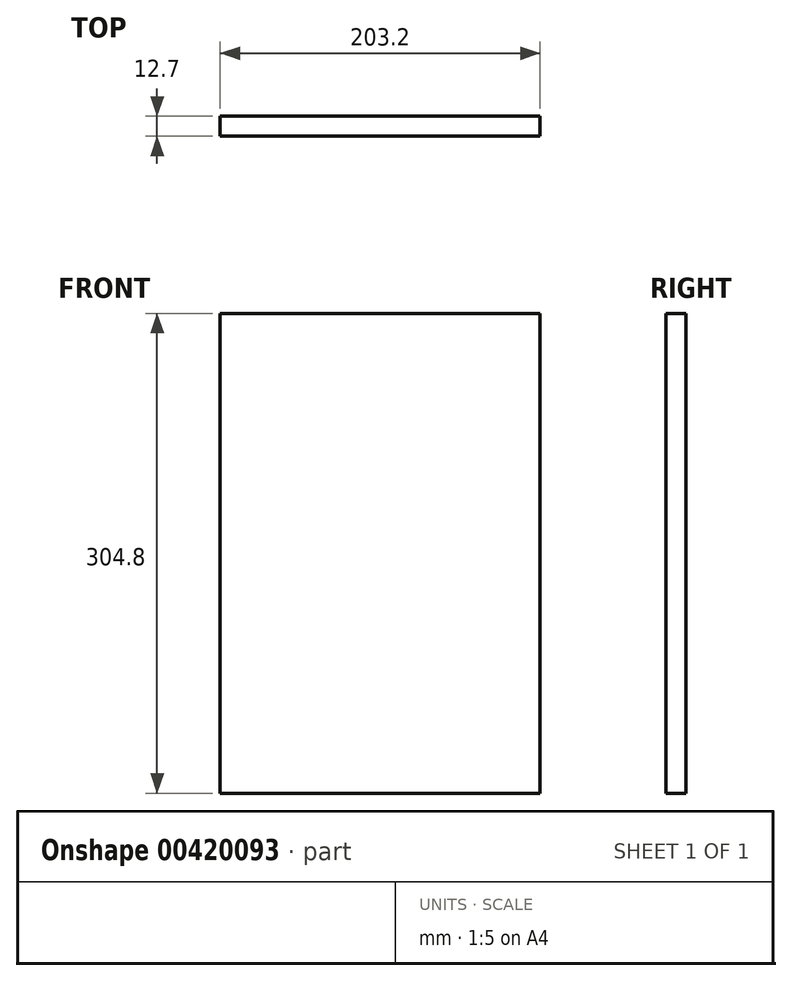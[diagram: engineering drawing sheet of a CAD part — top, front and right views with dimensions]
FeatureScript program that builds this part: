
annotation { "Feature Type Name" : "Feature", "Feature Type Description" : "" }
export const myFeature = defineFeature(function(context is Context, id is Id, definition is map)
    precondition{}
    {
        {
            var Q0;
            Q0=qCreatedBy(makeId("Front.planeOp"),FACE);
            var sketch = newSketch(context, id + "F0", { "sketchPlane" : qUnion([Q0])});
            skLineSegment(sketch, "E0.bottom", {"start": v(-107.05, 246.5) * mm, "end": v(96.15, 246.5) * mm});
            skLineSegment(sketch, "E0.top", {"start": v(-107.05, -58.3) * mm, "end": v(96.15, -58.3) * mm});
            skLineSegment(sketch, "E0.left", {"start": v(-107.05, 246.5) * mm, "end": v(-107.05, -58.3) * mm});
            skLineSegment(sketch, "E0.right", {"start": v(96.15, 246.5) * mm, "end": v(96.15, -58.3) * mm});
            skSolve(sketch);
        }
        {
            var Q0;
            Q0=makeQuery(id+"F0.imprint","IMPRINT",FACE,{"disambiguationData":[TD([[makeQuery(id+"F0.imprint","IMPRINT",EDGE,{"derivedFrom":sQuery(id+"F0.wireOp",EDGE,"E0.bottom")}),-1.0]])]});
            extrude(context, id + "F1", {"entities" : qUnion([Q0]), "depth" : 12.7 * mm});
        }
    });
